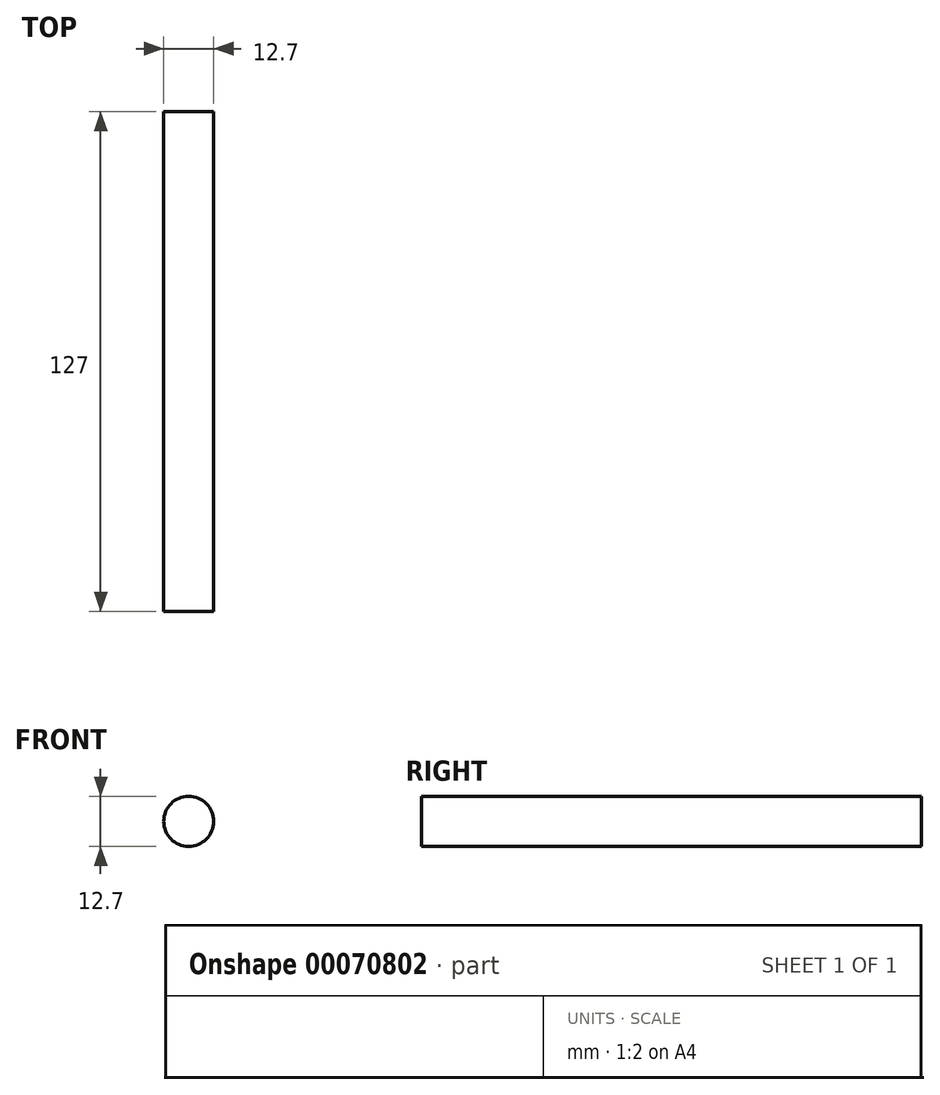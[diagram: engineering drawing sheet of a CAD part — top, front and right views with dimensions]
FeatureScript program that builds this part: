
annotation { "Feature Type Name" : "Feature", "Feature Type Description" : "" }
export const myFeature = defineFeature(function(context is Context, id is Id, definition is map)
    precondition{}
    {
        {
            var Q0;
            Q0=qCreatedBy(makeId("Front.planeOp"),FACE);
            var sketch = newSketch(context, id + "F0", { "sketchPlane" : qUnion([Q0])});
            skCircle(sketch, "E0", {"center": v(-4.64, 48.61) * mm, "radius": 6.35 * mm});
            skSolve(sketch);
        }
        {
            var Q0;
            Q0=makeQuery(id+"F0.imprint","IMPRINT",FACE,{"disambiguationData":[TD([[makeQuery(id+"F0.imprint","IMPRINT",EDGE,{"derivedFrom":sQuery(id+"F0.wireOp",EDGE,"E0")}),1.0]])]});
            extrude(context, id + "F1", {"entities" : qUnion([Q0]), "depth" : 127 * mm});
        }
    });
